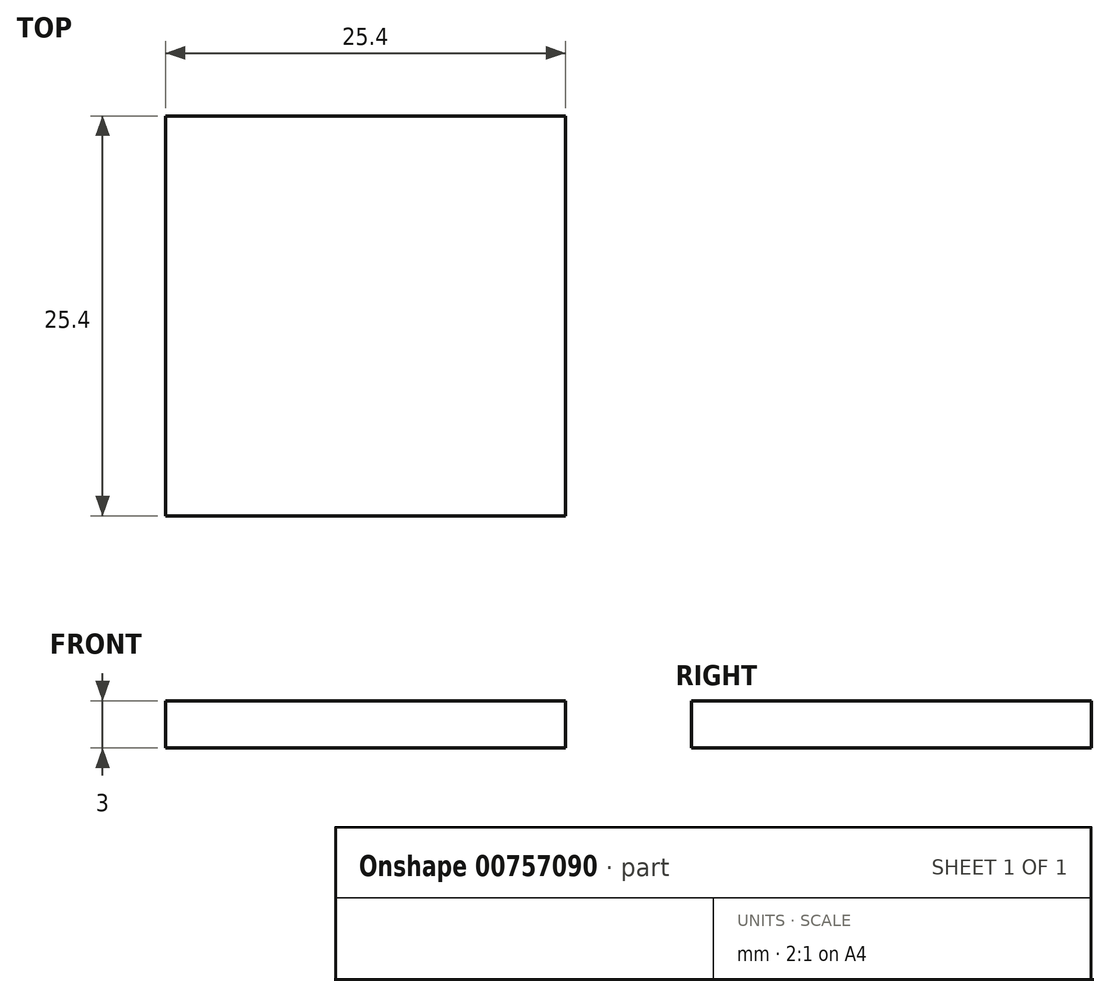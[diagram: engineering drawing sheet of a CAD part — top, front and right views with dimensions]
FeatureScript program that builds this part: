
annotation { "Feature Type Name" : "Feature", "Feature Type Description" : "" }
export const myFeature = defineFeature(function(context is Context, id is Id, definition is map)
    precondition{}
    {
        {
            var Q0;
            Q0=qCreatedBy(makeId("Top.planeOp"),FACE);
            var sketch = newSketch(context, id + "F0", { "sketchPlane" : qUnion([Q0])});
            skLineSegment(sketch, "E0.bottom", {"start": v(0, 0) * mm, "end": v(25.4, 0) * mm});
            skLineSegment(sketch, "E0.top", {"start": v(0, 25.4) * mm, "end": v(25.4, 25.4) * mm});
            skLineSegment(sketch, "E0.left", {"start": v(0, 0) * mm, "end": v(0, 25.4) * mm});
            skLineSegment(sketch, "E0.right", {"start": v(25.4, 0) * mm, "end": v(25.4, 25.4) * mm});
            skSolve(sketch);
        }
        {
            var Q0;
            Q0=makeQuery(id+"F0.imprint","IMPRINT",FACE,{"disambiguationData":[TD([[makeQuery(id+"F0.imprint","IMPRINT",EDGE,{"derivedFrom":sQuery(id+"F0.wireOp",EDGE,"E0.bottom")}),1.0]])]});
            extrude(context, id + "F1", {"entities" : qUnion([Q0]), "depth" : 3 * mm, "offsetDistance" : 25 * mm});
        }
    });
